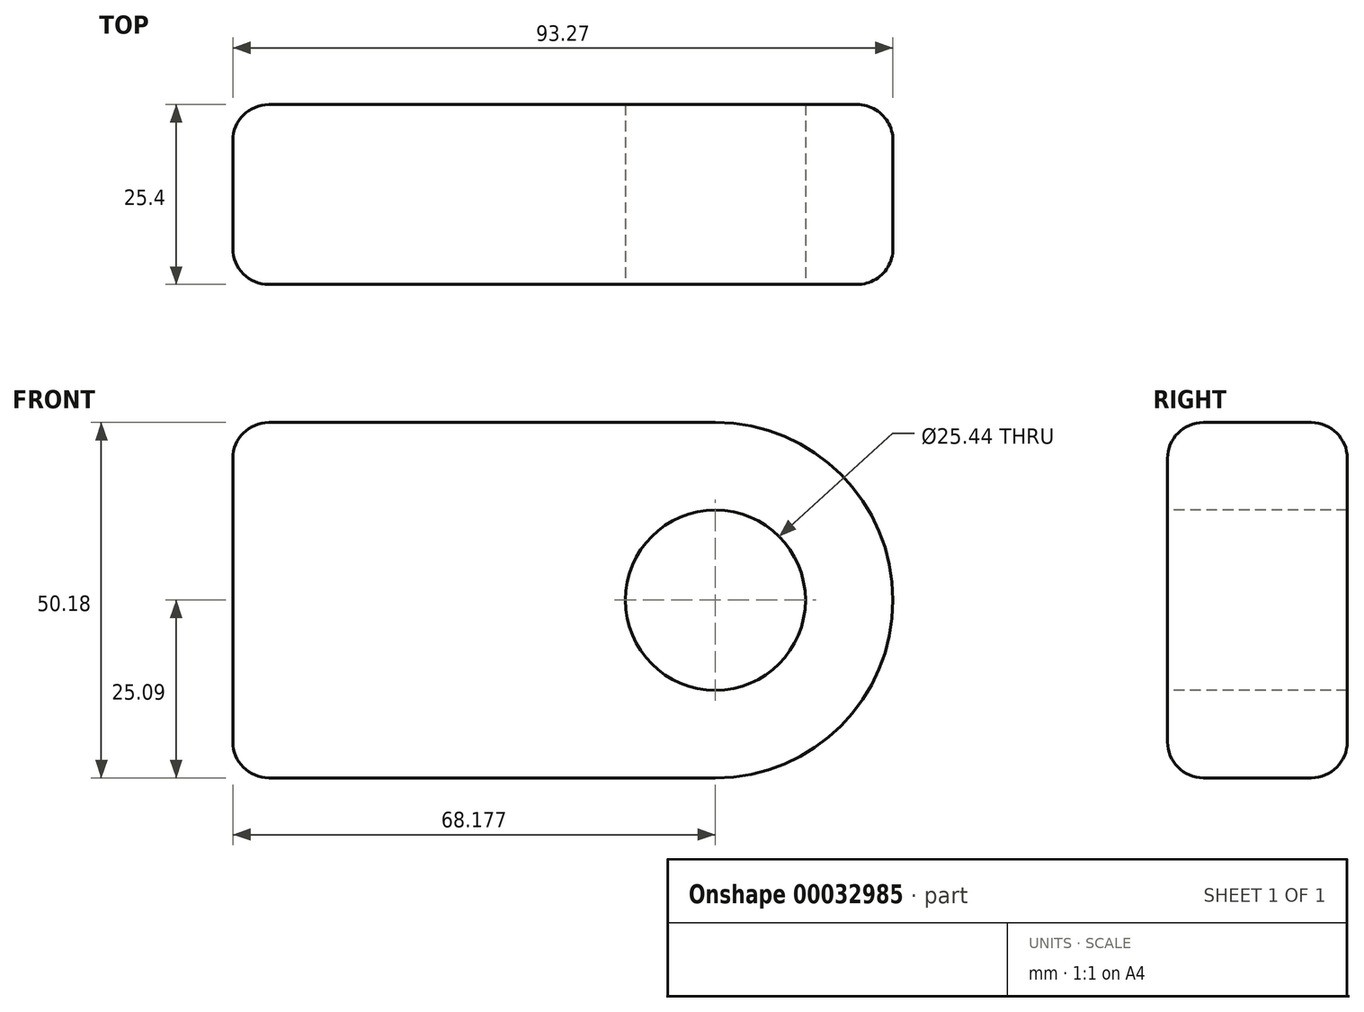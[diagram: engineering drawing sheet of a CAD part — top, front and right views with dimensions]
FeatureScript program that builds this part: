
annotation { "Feature Type Name" : "Feature", "Feature Type Description" : "" }
export const myFeature = defineFeature(function(context is Context, id is Id, definition is map)
    precondition{}
    {
        {
            var Q0;
            Q0=qCreatedBy(makeId("Front.planeOp"),FACE);
            var sketch = newSketch(context, id + "F0", { "sketchPlane" : qUnion([Q0])});
            skLineSegment(sketch, "E0.rect.bottom", {"start": v(34.09, -25.1) * mm, "end": v(34.09, -25.1) * mm});
            skLineSegment(sketch, "E0.rect.top", {"start": v(34.09, 25.1) * mm, "end": v(-34.09, 25.1) * mm});
            skLineSegment(sketch, "E0.rect.right", {"start": v(-34.09, -25.1) * mm, "end": v(-34.09, 25.1) * mm});
            skPoint(sketch, "E0.rect.middle", {"position": v(0, 0) * mm});
            skArc(sketch, "E1", {"start": v(34.09, -25.1) * mm, "mid": v(59.18, 0) * mm, "end": v(34.09, 25.1) * mm});
            skLineSegment(sketch, "E2", {"start": v(34.09, -25.1) * mm, "end": v(-34.09, -25.1) * mm});
            skLineSegment(sketch, "E3", {"start": v(34.09, 25.1) * mm, "end": v(34.09, 25.1) * mm});
            skSolve(sketch);
        }
        {
            var Q0;
            Q0=makeQuery(id+"F0.imprint","IMPRINT",FACE,{"disambiguationData":[TD([[makeQuery(id+"F0.imprint","IMPRINT",EDGE,{"derivedFrom":sQuery(id+"F0.wireOp",EDGE,"E0.rect.top")}),1.0]])]});
            extrude(context, id + "F1", {"entities" : qUnion([Q0]), "depth" : 25.4 * mm});
        }
        {
            var Q0;
            Q0=makeQuery(id+"F1.opExtrude","CAP_EDGE",EDGE,{"disambiguationData":[OSD([sQuery(id+"F0.wireOp",EDGE,"E0.rect.top")])],"isStart":false});
            var Q1;
            Q1=makeQuery(id+"F1.opExtrude","CAP_EDGE",EDGE,{"disambiguationData":[OSD([sQuery(id+"F0.wireOp",EDGE,"E0.rect.right")])],"isStart":false});
            var Q2;
            Q2=makeQuery(id+"F1.opExtrude","CAP_EDGE",EDGE,{"disambiguationData":[OSD([sQuery(id+"F0.wireOp",EDGE,"E2")])],"isStart":true});
            var Q3;
            Q3=makeQuery(id+"F1.opExtrude","CAP_EDGE",EDGE,{"disambiguationData":[OSD([sQuery(id+"F0.wireOp",EDGE,"E0.rect.right")])],"isStart":true});
            var Q4;
            Q4=makeQuery(id+"F1.opExtrude","SWEPT_EDGE",EDGE,{"disambiguationData":[OSD([sQuery(id+"F0.wireOp",EDGE,"E0.rect.right"),sQuery(id+"F0.wireOp",EDGE,"E2")])]});
            var Q5;
            Q5=makeQuery(id+"F1.opExtrude","SWEPT_EDGE",EDGE,{"disambiguationData":[OSD([sQuery(id+"F0.wireOp",EDGE,"E0.rect.top"),sQuery(id+"F0.wireOp",EDGE,"E0.rect.right")])]});
            fillet(context, id + "F2", {"entities" : qUnion([Q0, Q1, Q2, Q3, Q4, Q5]), "radius" : 5.08 * mm, "tangentPropagation" : true, "allowEdgeOverflow" : false});
        }
        {
            var Q0;
            Q0=makeQuery(id+"F1.opExtrude","CAP_FACE",FACE,{"disambiguationData":[OSD([sQuery(id+"F0.wireOp",EDGE,"E0.rect.top"),sQuery(id+"F0.wireOp",EDGE,"E0.rect.right"),sQuery(id+"F0.wireOp",EDGE,"E1"),sQuery(id+"F0.wireOp",EDGE,"E2")])],"isStart":false});
            var sketch = newSketch(context, id + "F3", { "sketchPlane" : qUnion([Q0])});
            skCircle(sketch, "E4", {"center": v(34.09, 0) * mm, "radius": 12.72 * mm});
            skSolve(sketch);
        }
        {
            var Q0;
            Q0=makeQuery(id+"F3.imprint","IMPRINT",FACE,{"disambiguationData":[TD([[makeQuery(id+"F3.imprint","IMPRINT",EDGE,{"derivedFrom":sQuery(id+"F3.wireOp",EDGE,"E4")}),1.0]])]});
            extrude(context, id + "F4", {"entities" : qUnion([Q0]), "operationType" : NewBodyOperationType.REMOVE, "endBound" : BoundingType.THROUGH_ALL, "oppositeDirection" : true, "depth" : 25.4 * mm});
        }
    });
